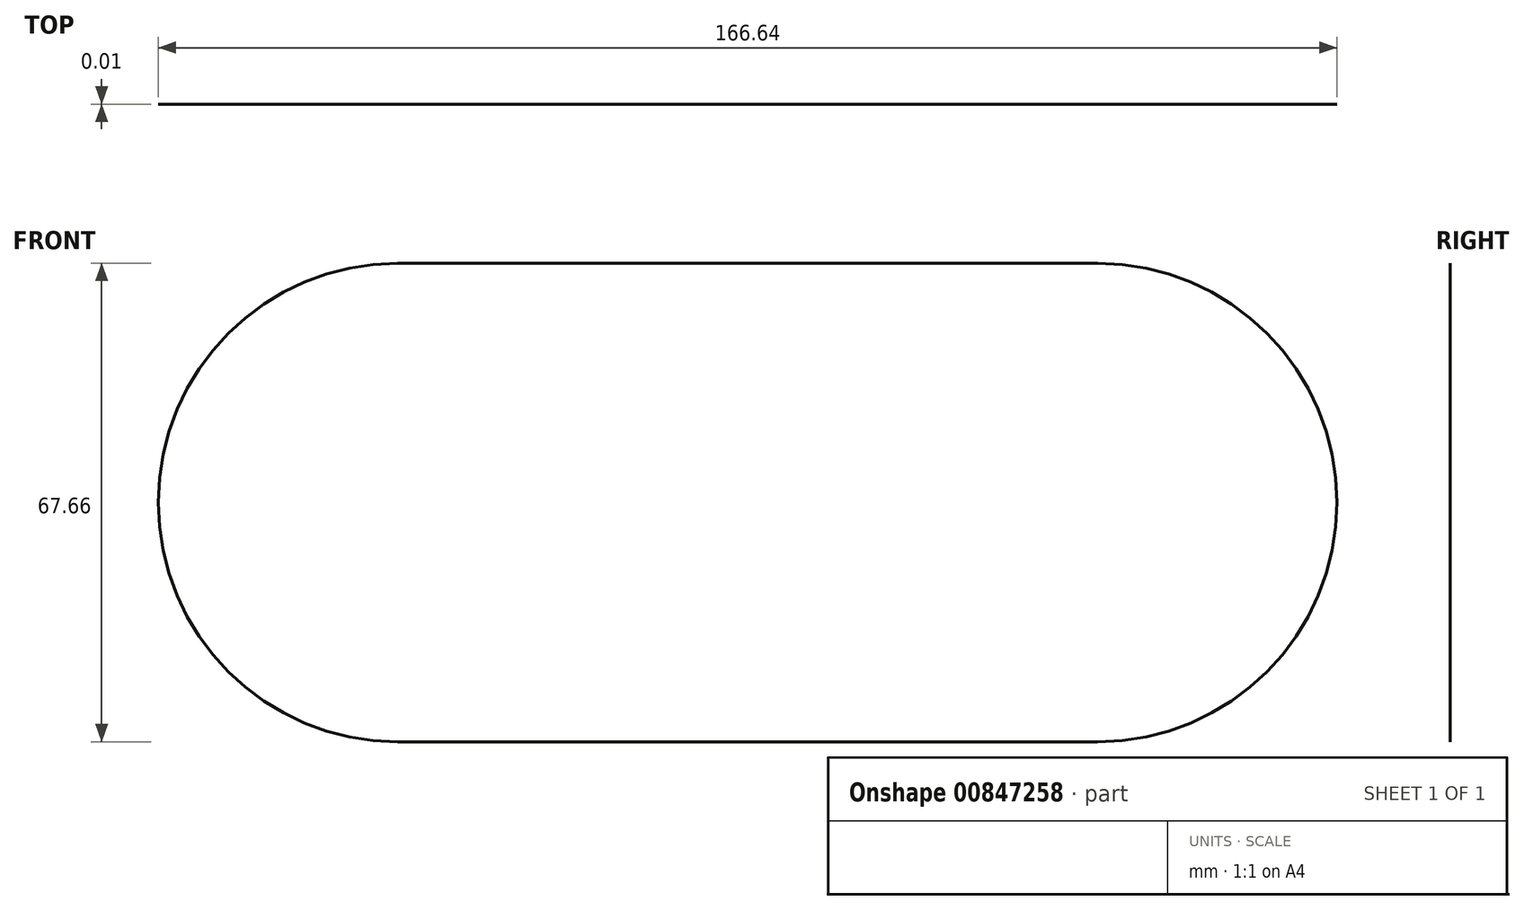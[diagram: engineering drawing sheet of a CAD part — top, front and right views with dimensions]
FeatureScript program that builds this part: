
annotation { "Feature Type Name" : "Feature", "Feature Type Description" : "" }
export const myFeature = defineFeature(function(context is Context, id is Id, definition is map)
    precondition{}
    {
        {
            var Q0;
            Q0=qCreatedBy(makeId("Front.planeOp"),FACE);
            var sketch = newSketch(context, id + "F0", { "sketchPlane" : qUnion([Q0])});
            skLineSegment(sketch, "E0", {"start": v(-49.48, -55.87) * mm, "end": v(-49.48, 56.1) * mm, "construction": true});
            skArc(sketch, "E1", {"start": v(-49.48, 33.83) * mm, "mid": v(-83.32, 0) * mm, "end": v(-49.48, -33.83) * mm});
            skLineSegment(sketch, "E2", {"start": v(-49.48, 33.83) * mm, "end": v(0, 33.83) * mm});
            skLineSegment(sketch, "E3", {"start": v(-49.48, -33.83) * mm, "end": v(0, -33.83) * mm});
            skLineSegment(sketch, "E4.MirrorCS", {"start": v(49.48, 33.83) * mm, "end": v(0, 33.83) * mm});
            skLineSegment(sketch, "E5.MirrorCS", {"start": v(49.48, -55.87) * mm, "end": v(49.48, 56.1) * mm, "construction": true});
            skArc(sketch, "E6.MirrorCS", {"start": v(49.48, 33.83) * mm, "mid": v(83.32, 0) * mm, "end": v(49.48, -33.83) * mm});
            skLineSegment(sketch, "E7.MirrorCS", {"start": v(49.48, -33.83) * mm, "end": v(0, -33.83) * mm});
            skSolve(sketch);
        }
        {
            var Q0;
            Q0=makeQuery(id+"F0.imprint","IMPRINT",FACE,{"disambiguationData":[TD([[makeQuery(id+"F0.imprint","IMPRINT",EDGE,{"derivedFrom":sQuery(id+"F0.wireOp",EDGE,"E1")}),1.0]])]});
            extrude(context, id + "F1", {"entities" : qUnion([Q0]), "depth" : 3 / 406.4 * mm, "offsetDistance" : 25.4 * mm, "hasDraft" : true, "draftAngle" : 3 * degree});
        }
    });
